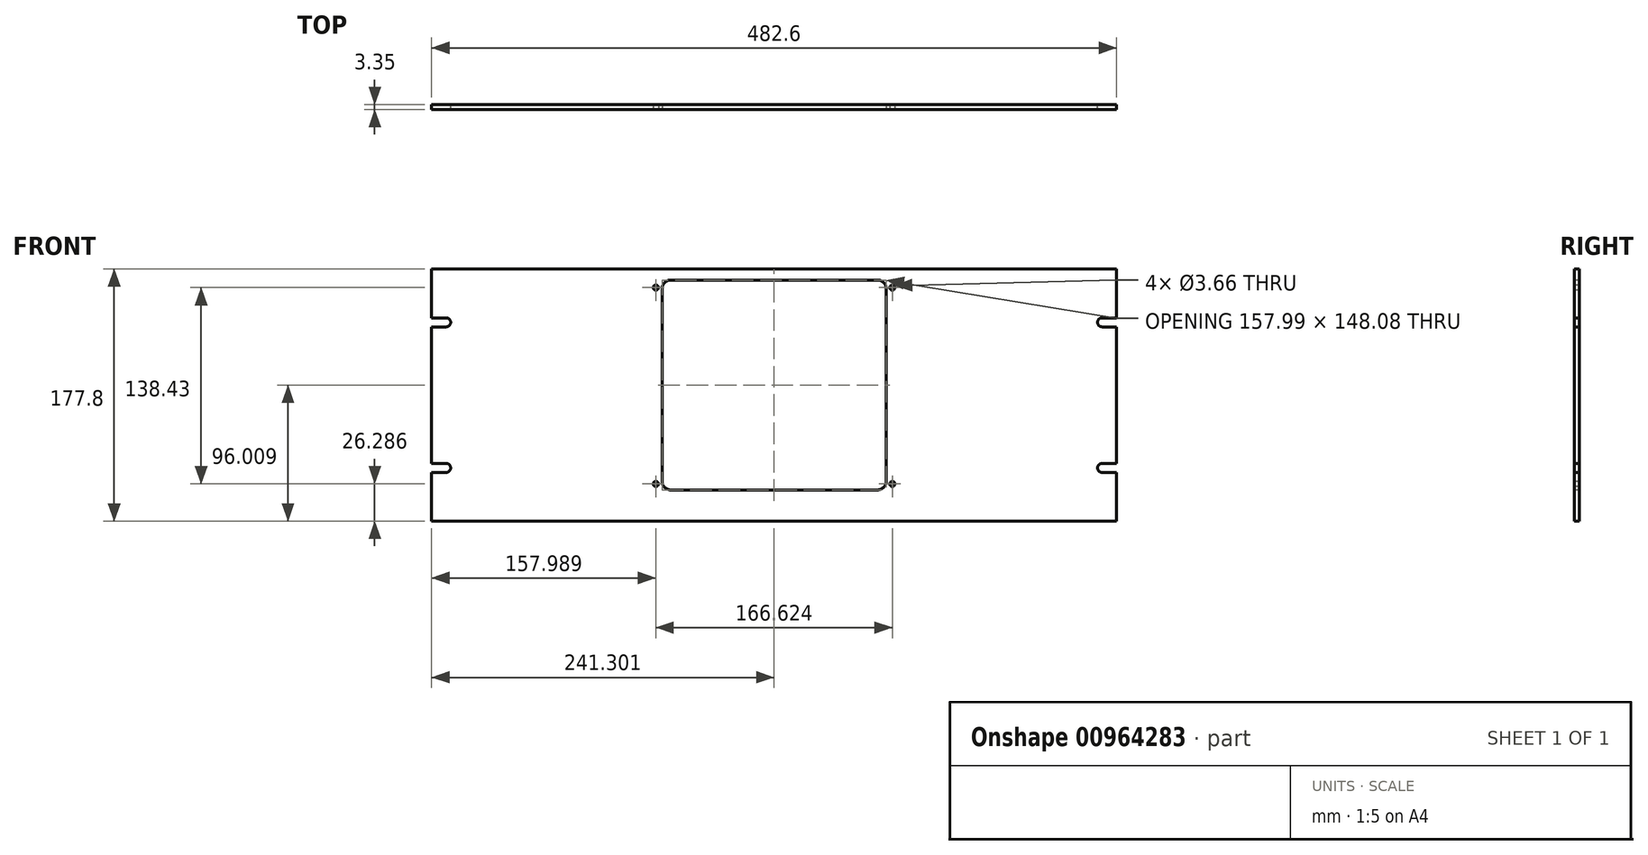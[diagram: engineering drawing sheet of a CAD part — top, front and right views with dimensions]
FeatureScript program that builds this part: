
annotation { "Feature Type Name" : "Feature", "Feature Type Description" : "" }
export const myFeature = defineFeature(function(context is Context, id is Id, definition is map)
    precondition{}
    {
        {
            var Q0;
            Q0=qCreatedBy(makeId("Front.planeOp"),FACE);
            var sketch = newSketch(context, id + "F0", { "sketchPlane" : qUnion([Q0])});
            skLineSegment(sketch, "E0.bottom", {"start": v(-256.05, -152.51) * mm, "end": v(226.55, -152.51) * mm});
            skLineSegment(sketch, "E0.top", {"start": v(-256.05, 25.29) * mm, "end": v(226.55, 25.29) * mm});
            skLineSegment(sketch, "E0.left", {"start": v(-256.05, -152.51) * mm, "end": v(-256.05, -118.1) * mm});
            skLineSegment(sketch, "E0.right", {"start": v(226.55, -152.51) * mm, "end": v(226.55, -118.1) * mm});
            skPoint(sketch, "E1", {"position": v(-245.76, -12.3) * mm});
            skLineSegment(sketch, "E2", {"start": v(-256.05, -63.61) * mm, "end": v(-239.44, -63.61) * mm, "construction": true});
            skLineSegment(sketch, "E3", {"start": v(-14.75, 38.2) * mm, "end": v(-14.75, 25.29) * mm, "construction": true});
            skLineSegment(sketch, "E4", {"start": v(-245.76, -12.3) * mm, "end": v(-256.05, -12.3) * mm, "construction": true});
            skArc(sketch, "E5.0.startCap", {"start": v(-245.76, -9.13) * mm, "mid": v(-242.59, -12.3) * mm, "end": v(-245.76, -15.48) * mm});
            skLineSegment(sketch, "E5.0.left", {"start": v(-245.76, -15.48) * mm, "end": v(-256.05, -15.48) * mm});
            skLineSegment(sketch, "E5.0.right", {"start": v(-245.76, -9.13) * mm, "end": v(-256.05, -9.13) * mm});
            skLineSegment(sketch, "E6.trimOffspring", {"start": v(-256.05, -9.13) * mm, "end": v(-256.05, 25.29) * mm});
            skArc(sketch, "E7.MirrorCS", {"start": v(-245.76, -118.1) * mm, "mid": v(-242.59, -114.92) * mm, "end": v(-245.76, -111.75) * mm});
            skLineSegment(sketch, "E8.MirrorCS", {"start": v(-245.76, -111.75) * mm, "end": v(-256.05, -111.75) * mm});
            skLineSegment(sketch, "E9.MirrorCS", {"start": v(-256.05, -118.1) * mm, "end": v(-256.05, -152.51) * mm});
            skLineSegment(sketch, "E10.MirrorCS", {"start": v(-245.76, -118.1) * mm, "end": v(-256.05, -118.1) * mm});
            skLineSegment(sketch, "E11.trimOffspring", {"start": v(-256.05, -111.75) * mm, "end": v(-256.05, -15.48) * mm});
            skArc(sketch, "E12.MirrorCS", {"start": v(216.26, -9.13) * mm, "mid": v(213.09, -12.3) * mm, "end": v(216.26, -15.48) * mm});
            skLineSegment(sketch, "E13.MirrorCS", {"start": v(216.26, -15.48) * mm, "end": v(226.55, -15.48) * mm});
            skLineSegment(sketch, "E14.MirrorCS", {"start": v(216.26, -9.13) * mm, "end": v(226.55, -9.13) * mm});
            skLineSegment(sketch, "E15.MirrorCS", {"start": v(216.26, -111.75) * mm, "end": v(226.55, -111.75) * mm});
            skArc(sketch, "E16.MirrorCS", {"start": v(216.26, -118.1) * mm, "mid": v(213.09, -114.92) * mm, "end": v(216.26, -111.75) * mm});
            skLineSegment(sketch, "E17.MirrorCS", {"start": v(216.26, -118.1) * mm, "end": v(226.55, -118.1) * mm});
            skLineSegment(sketch, "E18.trimOffspring", {"start": v(226.55, -9.13) * mm, "end": v(226.55, 25.29) * mm});
            skLineSegment(sketch, "E19.trimOffspring", {"start": v(226.55, -111.75) * mm, "end": v(226.55, -15.48) * mm});
            skSolve(sketch);
        }
        {
            var Q0;
            Q0=qSketchRegion(id+"F0",true);
            extrude(context, id + "F1", {"entities" : qUnion([Q0]), "depth" : 3.35 * mm, "offsetDistance" : 25.4 * mm});
        }
        {
            var Q0;
            Q0=makeQuery(id+"F1.opExtrude","CAP_FACE",FACE,{"disambiguationData":[OSD([sQuery(id+"F0.wireOp",EDGE,"E0.bottom"),sQuery(id+"F0.wireOp",EDGE,"E0.top"),sQuery(id+"F0.wireOp",EDGE,"E0.right"),sQuery(id+"F0.wireOp",EDGE,"E5.0.startCap"),sQuery(id+"F0.wireOp",EDGE,"E5.0.left"),sQuery(id+"F0.wireOp",EDGE,"E5.0.right"),sQuery(id+"F0.wireOp",EDGE,"E6.trimOffspring"),sQuery(id+"F0.wireOp",EDGE,"E7.MirrorCS"),sQuery(id+"F0.wireOp",EDGE,"E8.MirrorCS"),sQuery(id+"F0.wireOp",EDGE,"E9.MirrorCS"),sQuery(id+"F0.wireOp",EDGE,"E10.MirrorCS"),sQuery(id+"F0.wireOp",EDGE,"E11.trimOffspring"),sQuery(id+"F0.wireOp",EDGE,"E12.MirrorCS"),sQuery(id+"F0.wireOp",EDGE,"E13.MirrorCS"),sQuery(id+"F0.wireOp",EDGE,"E14.MirrorCS"),sQuery(id+"F0.wireOp",EDGE,"E15.MirrorCS"),sQuery(id+"F0.wireOp",EDGE,"E16.MirrorCS"),sQuery(id+"F0.wireOp",EDGE,"E17.MirrorCS"),sQuery(id+"F0.wireOp",EDGE,"E18.trimOffspring"),sQuery(id+"F0.wireOp",EDGE,"E19.trimOffspring")])],"isStart":false});
            var sketch = newSketch(context, id + "F2", { "sketchPlane" : qUnion([Q0])});
            skLineSegment(sketch, "E20.0", {"start": v(57.9, 17.54) * mm, "end": v(-87.4, 17.54) * mm});
            skArc(sketch, "E20.1", {"start": v(64.25, 11.2) * mm, "mid": v(62.39, 15.68) * mm, "end": v(57.9, 17.54) * mm});
            skArc(sketch, "E20.2", {"start": v(-87.4, 17.54) * mm, "mid": v(-91.88, 15.68) * mm, "end": v(-93.74, 11.2) * mm});
            skLineSegment(sketch, "E20.3", {"start": v(64.25, -124.2) * mm, "end": v(64.25, 11.2) * mm});
            skLineSegment(sketch, "E20.4", {"start": v(-93.74, 11.2) * mm, "end": v(-93.74, -124.2) * mm});
            skArc(sketch, "E20.5", {"start": v(-93.74, -124.2) * mm, "mid": v(-91.88, -128.68) * mm, "end": v(-87.4, -130.54) * mm});
            skLineSegment(sketch, "E20.6", {"start": v(-87.4, -130.54) * mm, "end": v(57.9, -130.54) * mm});
            skArc(sketch, "E20.7", {"start": v(57.9, -130.54) * mm, "mid": v(62.39, -128.68) * mm, "end": v(64.25, -124.2) * mm});
            skPoint(sketch, "E21.center.orphan", {"position": v(68.56, -126.22) * mm});
            skPoint(sketch, "E22.center.orphan", {"position": v(-98.06, -126.22) * mm});
            skPoint(sketch, "E23.center.orphan", {"position": v(-98.06, 12.2) * mm});
            skPoint(sketch, "E24.center.orphan", {"position": v(68.56, 12.2) * mm});
            skCircle(sketch, "E25.0", {"center": v(-98.06, 12.2) * mm, "radius": 2.16 * mm, "construction": true});
            skCircle(sketch, "E26.0", {"center": v(68.56, 12.2) * mm, "radius": 2.16 * mm, "construction": true});
            skCircle(sketch, "E27.0", {"center": v(68.56, -126.22) * mm, "radius": 2.16 * mm, "construction": true});
            skCircle(sketch, "E28.0", {"center": v(-98.06, -126.22) * mm, "radius": 2.16 * mm, "construction": true});
            skPoint(sketch, "E29.orphan", {"position": v(-14.75, 17.54) * mm});
            skPoint(sketch, "E30.orphan", {"position": v(-14.75, -130.54) * mm});
            skPoint(sketch, "E31.orphan", {"position": v(64.25, -56.5) * mm});
            skPoint(sketch, "E32.orphan", {"position": v(-93.74, -56.5) * mm});
            skSolve(sketch);
        }
        {
            var Q0;
            Q0 = qSketchRegion(id + "F2", true);
            extrude(context, id + "F3", {"entities" : qUnion([Q0]), "operationType" : NewBodyOperationType.REMOVE, "endBound" : BoundingType.UP_TO_NEXT, "oppositeDirection" : true, "depth" : 25.4 * mm, "offsetDistance" : 25.4 * mm});
        }
        {
            var Q0;
            Q0=sQuery(id+"F2.wireOp",VERTEX,"E22.center.orphan");
            var Q1;
            Q1=sQuery(id+"F2.wireOp",VERTEX,"E21.center.orphan");
            var Q2;
            Q2=sQuery(id+"F2.wireOp",VERTEX,"E24.center.orphan");
            var Q3;
            Q3=sQuery(id+"F2.wireOp",VERTEX,"E23.center.orphan");
            var Q4;
            Q4=makeQuery(id+"F1.opExtrude","SWEPT_BODY",BODY,{"disambiguationData":[OSD([sQuery(id+"F0.wireOp",EDGE,"E0.bottom"),sQuery(id+"F0.wireOp",EDGE,"E0.top"),sQuery(id+"F0.wireOp",EDGE,"E0.left"),sQuery(id+"F0.wireOp",EDGE,"E0.right"),sQuery(id+"F0.wireOp",EDGE,"E5.0.startCap"),sQuery(id+"F0.wireOp",EDGE,"E5.0.left"),sQuery(id+"F0.wireOp",EDGE,"E5.0.right"),sQuery(id+"F0.wireOp",EDGE,"E6.trimOffspring"),sQuery(id+"F0.wireOp",EDGE,"E7.MirrorCS"),sQuery(id+"F0.wireOp",EDGE,"E8.MirrorCS"),sQuery(id+"F0.wireOp",EDGE,"E10.MirrorCS"),sQuery(id+"F0.wireOp",EDGE,"E11.trimOffspring"),sQuery(id+"F0.wireOp",EDGE,"E12.MirrorCS"),sQuery(id+"F0.wireOp",EDGE,"E13.MirrorCS"),sQuery(id+"F0.wireOp",EDGE,"E14.MirrorCS"),sQuery(id+"F0.wireOp",EDGE,"E15.MirrorCS"),sQuery(id+"F0.wireOp",EDGE,"E16.MirrorCS"),sQuery(id+"F0.wireOp",EDGE,"E17.MirrorCS"),sQuery(id+"F0.wireOp",EDGE,"E18.trimOffspring"),sQuery(id+"F0.wireOp",EDGE,"E19.trimOffspring")])]});
            hole(context, id + "F4", {"style" : HoleStyle.SIMPLE, "endStyle" : HoleEndStyle.THROUGH, "standardTappedOrClearance" : lookupTablePath({ "fit" : "Close", "standard" : "ANSI", "size" : "#6", "type" : "Clearance" }), "standardBlindInLast" : lookupTablePath({ "fit" : "Close", "standard" : "ANSI", "engagement" : "75%", "pitch" : "32 tpi", "size" : "#6", "type" : "Clearance & tapped" }), "holeDiameter" : 3.66 * mm, "majorDiameter" : 6.35 * mm, "isTappedThrough" : true, "tappedDepth" : 12.7 * mm, "tapClearance" : 3, "locations" : qUnion([Q0, Q1, Q2, Q3]), "scope" : qUnion([Q4])});
        }
    });
